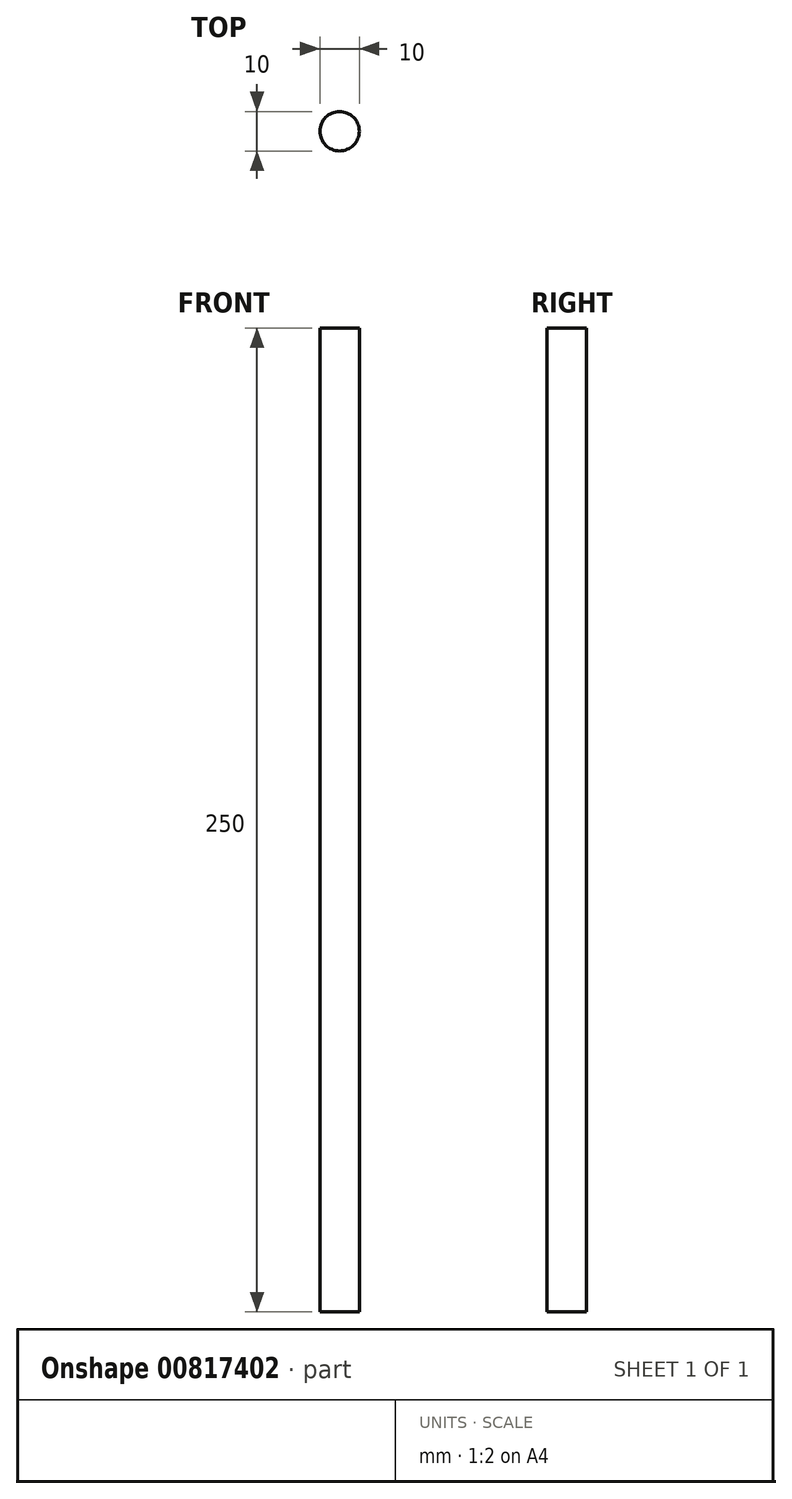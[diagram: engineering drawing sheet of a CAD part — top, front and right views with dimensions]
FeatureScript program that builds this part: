
annotation { "Feature Type Name" : "Feature", "Feature Type Description" : "" }
export const myFeature = defineFeature(function(context is Context, id is Id, definition is map)
    precondition{}
    {
        {
            var Q0;
            Q0=qCreatedBy(makeId("Top.planeOp"),FACE);
            var sketch = newSketch(context, id + "F0", { "sketchPlane" : qUnion([Q0])});
            skCircle(sketch, "E0", {"center": v(0, 0) * mm, "radius": 5 * mm});
            skSolve(sketch);
        }
        {
            var Q0;
            Q0=makeQuery(id+"F0.imprint","IMPRINT",FACE,{"disambiguationData":[TD([[makeQuery(id+"F0.imprint","IMPRINT",EDGE,{"derivedFrom":sQuery(id+"F0.wireOp",EDGE,"E0")}),1.0]])]});
            extrude(context, id + "F1", {"entities" : qUnion([Q0]), "depth" : 250 * mm, "offsetDistance" : 25 * mm});
        }
    });
